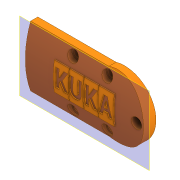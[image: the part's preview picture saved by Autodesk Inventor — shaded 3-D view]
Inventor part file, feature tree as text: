
AUTODESK INVENTOR PART (.ipt)
format: ipt  version: 2020 (Build 240168000, 168)  size: 460,800 bytes
history: native  units: in
note: dims shown in document units (in); Inventor stores cm internally (conversion verified against a paired STEP export)
features: sketch x9, extrude x8, plane x2, fillet x1, emboss x1, projected_geometry x1
ambient origin geometry x8: Origin, YZ Plane, XZ Plane, XY Plane, X Axis, Y Axis, Z Axis, Center Point
bodies: Solid1 (feature_tree)
feature tree (22):
  extrude  "Extrusion1"  Depth=0.2362in
  extrude  "Extrusion2"  Depth=0.2362in
  extrude  "Extrusion3"  Depth=0.2362in
  fillet  "Fillet1"  Radius=0.2264in
  plane  "Work Plane1"
  extrude  "Extrusion4"  Depth=0.1969in
  sketch  "Sketch5"  dims[d11=0.0in d12=0.0in d13=0.0787in]
  extrude  "Extrusion5"  Depth=0.0787in
  extrude  "Extrusion6"  Depth=0.5512in
  extrude  "Extrusion7"  Depth=0.9843in
  emboss  "Emboss1"
  plane  "Work Plane2"
  extrude  "Extrusion8"  Depth=0.0197in
  sketch  "Sketch1"  dims[d0=0.1575in d1=0.2362in]
  sketch  "Sketch2"  dims[d2=0.2362in d3=0.2362in]
  sketch  "Sketch3"  dims[d4=0.2362in d5=0.2362in d6=0.2264in d7=0.0in]
  sketch  "Sketch4"  dims[d8=0.1969in d9=0.0in d10=0.1969in]
  projected_geometry  "Projected Loop1"
  sketch  "Sketch6"  dims[d14=0.5512in d15=0.5512in]
  sketch  "Sketch7"  dims[d16=0.9843in d17=0.9843in]
  sketch  "Sketch8"  dims[d18=0.0787in d19=0.0in d20=0.0197in]
  sketch  "Sketch9"  dims[d21=0.0197in d22=0.0197in d23=0.0in d24=0.0in d25=0.0787in d26=0.0in d27=0.0in d28=0.0in d29=0.0394in d30=0.0in d31=0.3543in d32=0.3543in d33=0.3543in d34=0.3543in d35=0.3543in d36=0.4724in d37=0.0in]
